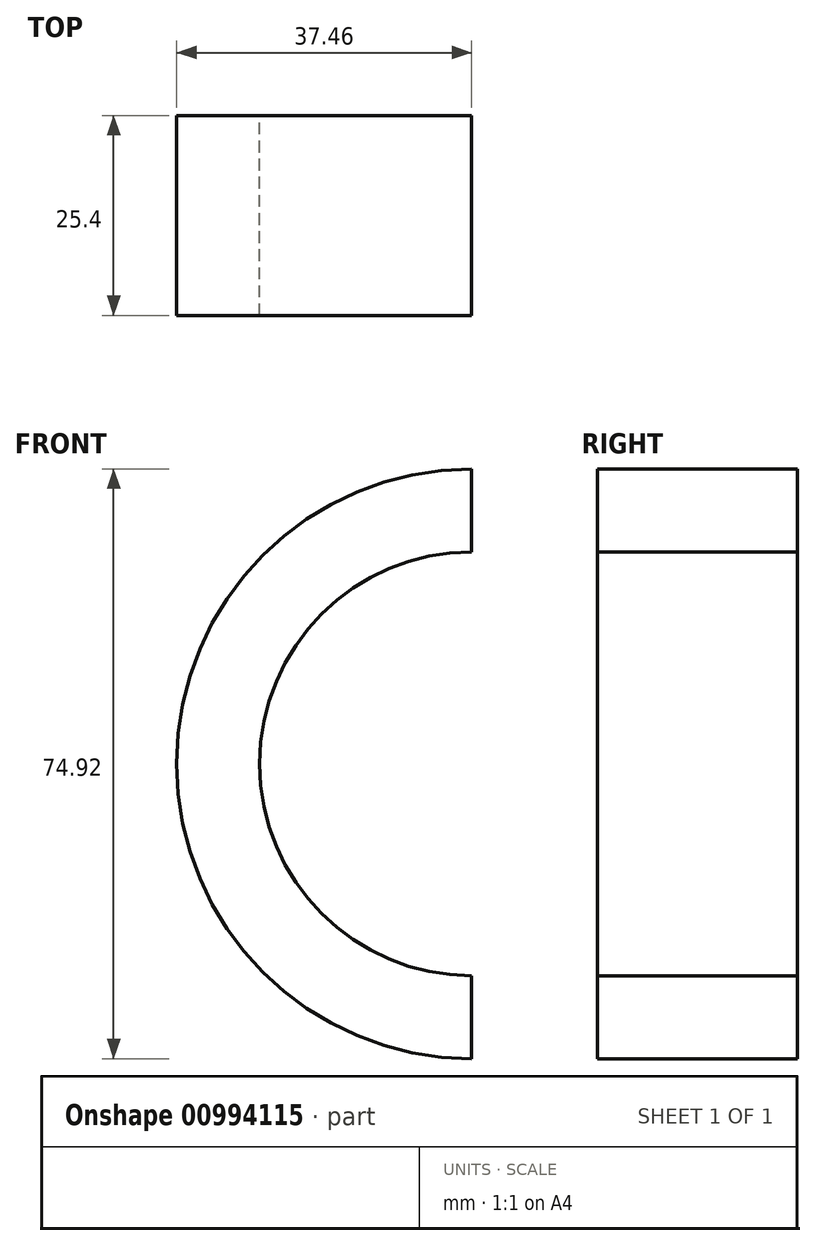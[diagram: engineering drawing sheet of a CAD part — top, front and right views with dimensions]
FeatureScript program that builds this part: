
annotation { "Feature Type Name" : "Feature", "Feature Type Description" : "" }
export const myFeature = defineFeature(function(context is Context, id is Id, definition is map)
    precondition{}
    {
        {
            var Q0;
            Q0=qCreatedBy(makeId("Front.planeOp"),FACE);
            var sketch = newSketch(context, id + "F0", { "sketchPlane" : qUnion([Q0])});
            skCircle(sketch, "E0", {"center": v(0, 0) * mm, "radius": 26.92 * mm});
            skCircle(sketch, "E1", {"center": v(0, 0) * mm, "radius": 37.47 * mm});
            skSolve(sketch);
        }
        {
            var Q0;
            Q0 = qSketchRegion(id + "F0", true);
            extrude(context, id + "F1", {"entities" : qUnion([Q0]), "depth" : 25.4 * mm, "offsetDistance" : 25.4 * mm});
        }
        {
            var Q0;
            Q0=makeQuery(id+"F1.opExtrude","CAP_FACE",FACE,{"disambiguationData":[OSD([sQuery(id+"F0.wireOp",EDGE,"E0"),sQuery(id+"F0.wireOp",EDGE,"E1")])],"isStart":false});
            var sketch = newSketch(context, id + "F2", { "sketchPlane" : qUnion([Q0])});
            skLineSegment(sketch, "E2.bottom", {"start": v(0, 0) * mm, "end": v(43.23, 0) * mm});
            skLineSegment(sketch, "E2.top", {"start": v(0, 39.54) * mm, "end": v(43.23, 39.54) * mm});
            skLineSegment(sketch, "E2.left", {"start": v(0, 0) * mm, "end": v(0, 39.54) * mm});
            skLineSegment(sketch, "E2.right", {"start": v(43.23, 0) * mm, "end": v(43.23, 39.54) * mm});
            skLineSegment(sketch, "E3.bottom", {"start": v(0, 0) * mm, "end": v(42.77, 0) * mm});
            skLineSegment(sketch, "E3.top", {"start": v(0, -133.74) * mm, "end": v(42.77, -133.74) * mm});
            skLineSegment(sketch, "E3.left", {"start": v(0, 0) * mm, "end": v(0, -133.74) * mm});
            skLineSegment(sketch, "E3.right", {"start": v(42.77, 0) * mm, "end": v(42.77, -133.74) * mm});
            skSolve(sketch);
        }
        {
            var Q0;
            Q0 = qSketchRegion(id + "F2", true);
            extrude(context, id + "F3", {"entities" : qUnion([Q0]), "operationType" : NewBodyOperationType.REMOVE, "endBound" : BoundingType.THROUGH_ALL, "oppositeDirection" : true, "depth" : 25.4 * mm, "offsetDistance" : 25.4 * mm});
        }
    });
